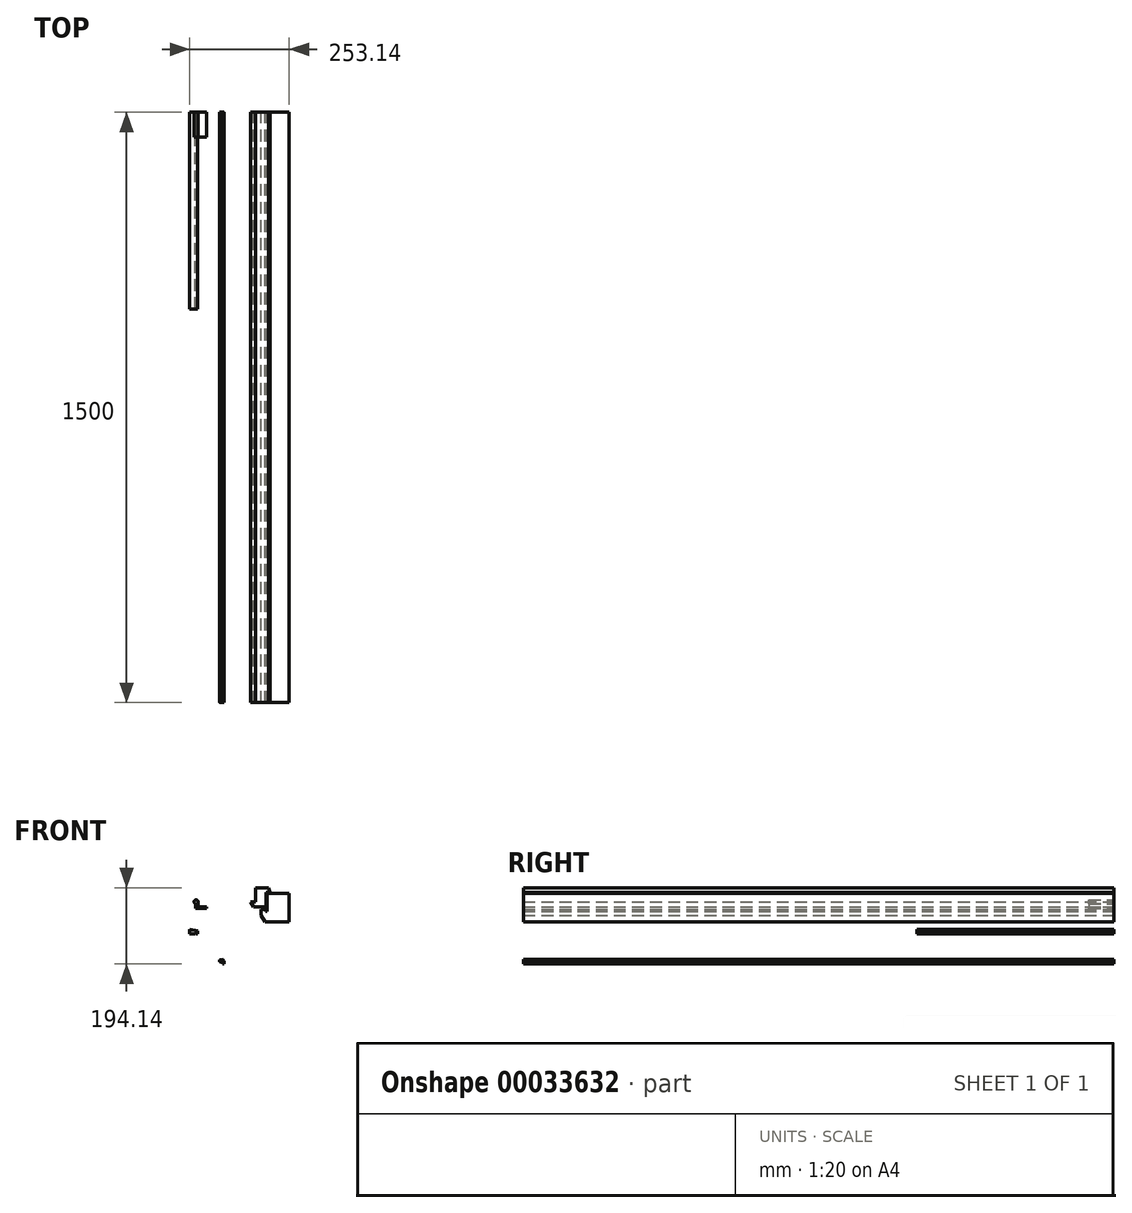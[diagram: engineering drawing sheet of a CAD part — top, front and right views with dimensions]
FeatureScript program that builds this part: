
annotation { "Feature Type Name" : "Feature", "Feature Type Description" : "" }
export const myFeature = defineFeature(function(context is Context, id is Id, definition is map)
    precondition{}
    {
        {
            var Q0;
            Q0=qCreatedBy(makeId("Front.planeOp"),FACE);
            var sketch = newSketch(context, id + "F0", { "sketchPlane" : qUnion([Q0])});
            skLineSegment(sketch, "E0.bottom", {"start": v(-57, 72) * mm, "end": v(0, 72) * mm});
            skLineSegment(sketch, "E0.top", {"start": v(-62, 0) * mm, "end": v(0, 0) * mm});
            skLineSegment(sketch, "E0.left", {"start": v(-72, 32) * mm, "end": v(-72, 17) * mm});
            skLineSegment(sketch, "E0.right", {"start": v(0, 72) * mm, "end": v(0, 0) * mm});
            skLineSegment(sketch, "E1.top", {"start": v(-72, 32) * mm, "end": v(-60, 32) * mm});
            skLineSegment(sketch, "E1.right", {"start": v(-57, 72) * mm, "end": v(-57, 32) * mm});
            skLineSegment(sketch, "E2", {"start": v(-72, 17) * mm, "end": v(-62, 0) * mm});
            skLineSegment(sketch, "E3", {"start": v(-57, 32) * mm, "end": v(-57, 26.5) * mm});
            skLineSegment(sketch, "E4", {"start": v(-57, 26.5) * mm, "end": v(-60, 26.5) * mm});
            skLineSegment(sketch, "E5", {"start": v(-60, 26.5) * mm, "end": v(-60, 32) * mm});
            skSolve(sketch);
        }
        {
            var Q0;
            Q0=qCreatedBy(makeId("Front.planeOp"),FACE);
            var sketch = newSketch(context, id + "F1", { "sketchPlane" : qUnion([Q0])});
            skLineSegment(sketch, "E6", {"start": v(-49, 75) * mm, "end": v(-59, 75) * mm});
            skLineSegment(sketch, "E7", {"start": v(-59, 75) * mm, "end": v(-59, 38) * mm});
            skLineSegment(sketch, "E8", {"start": v(-59, 38) * mm, "end": v(-91, 38) * mm});
            skLineSegment(sketch, "E9", {"start": v(-91, 38) * mm, "end": v(-98, 51) * mm});
            skLineSegment(sketch, "E10", {"start": v(-98, 51) * mm, "end": v(-86, 51) * mm});
            skLineSegment(sketch, "E11", {"start": v(-86, 51) * mm, "end": v(-86, 87) * mm});
            skLineSegment(sketch, "E12", {"start": v(-86, 87) * mm, "end": v(-53, 87) * mm});
            skLineSegment(sketch, "E13.0", {"start": v(-72, 38) * mm, "end": v(-57, 38) * mm, "construction": true});
            skLineSegment(sketch, "E14.0", {"start": v(-59, 72) * mm, "end": v(-59, 27) * mm, "construction": true});
            skLineSegment(sketch, "E15", {"start": v(-49, 75) * mm, "end": v(-53, 87) * mm});
            skSolve(sketch);
        }
        {
            var Q0;
            Q0=qCreatedBy(makeId("Front.planeOp"),FACE);
            var sketch = newSketch(context, id + "F2", { "sketchPlane" : qUnion([Q0])});
            skArc(sketch, "E16", {"start": v(-235.9, 46.13) * mm, "mid": v(-234.42, 46.6) * mm, "end": v(-233.15, 47.5) * mm});
            skLineSegment(sketch, "E17.0", {"start": v(-235.9, 46.13) * mm, "end": v(-235.9, 36.02) * mm});
            skLineSegment(sketch, "E18.0", {"start": v(-237.4, 46.13) * mm, "end": v(-237.4, 34.08) * mm});
            skLineSegment(sketch, "E19.0", {"start": v(-237.4, 34.08) * mm, "end": v(-210.4, 34.08) * mm});
            skLineSegment(sketch, "E20.0", {"start": v(-235.9, 36.02) * mm, "end": v(-210.4, 36.02) * mm});
            skLineSegment(sketch, "E21", {"start": v(-231.65, 51.08) * mm, "end": v(-231.65, 38.08) * mm});
            skLineSegment(sketch, "E22.trimOffspring", {"start": v(-231.65, 38.08) * mm, "end": v(-210.4, 38.08) * mm});
            skLineSegment(sketch, "E23", {"start": v(-210.4, 34.08) * mm, "end": v(-210.4, 36.02) * mm});
            skLineSegment(sketch, "E24.0", {"start": v(-233.15, 47.5) * mm, "end": v(-233.15, 36.58) * mm});
            skLineSegment(sketch, "E25.0", {"start": v(-233.15, 36.58) * mm, "end": v(-210.4, 36.58) * mm});
            skLineSegment(sketch, "E26", {"start": v(-210.4, 38.08) * mm, "end": v(-210.4, 36.58) * mm});
            skArc(sketch, "E27.trimOffspring", {"start": v(-231.65, 51.08) * mm, "mid": v(-239.9, 54.87) * mm, "end": v(-237.4, 46.13) * mm});
            skSolve(sketch);
        }
        {
            var Q0;
            Q0=makeQuery(id+"F0.imprint","IMPRINT",FACE,{"disambiguationData":[TD([[makeQuery(id+"F0.imprint","IMPRINT",EDGE,{"derivedFrom":sQuery(id+"F0.wireOp",EDGE,"E0.bottom")}),-1.0]])]});
            var Q1;
            Q1=makeQuery(id+"F1.imprint","IMPRINT",FACE,{"disambiguationData":[TD([[makeQuery(id+"F1.imprint","IMPRINT",EDGE,{"derivedFrom":sQuery(id+"F1.wireOp",EDGE,"E6")}),-1.0]])]});
            extrude(context, id + "F3", {"entities" : qUnion([Q0, Q1]), "depth" : 1500 * mm});
        }
        {
            var Q0;
            Q0=makeQuery(id+"F2.imprint","IMPRINT",FACE,{"disambiguationData":[TD([[makeQuery(id+"F2.imprint","IMPRINT",EDGE,{"derivedFrom":sQuery(id+"F2.wireOp",EDGE,"E16")}),1.0]])]});
            extrude(context, id + "F4", {"entities" : qUnion([Q0]), "depth" : 63 * mm});
        }
        {
            var Q0;
            Q0=qCreatedBy(makeId("Front.planeOp"),FACE);
            var sketch = newSketch(context, id + "F5", { "sketchPlane" : qUnion([Q0])});
            skLineSegment(sketch, "E28", {"start": v(-169.24, -107.14) * mm, "end": v(-166.24, -107.14) * mm});
            skLineSegment(sketch, "E29", {"start": v(-166.24, -107.14) * mm, "end": v(-166.24, -99.64) * mm});
            skLineSegment(sketch, "E30", {"start": v(-166.74, -99.14) * mm, "end": v(-173.95, -99.14) * mm});
            skLineSegment(sketch, "E31", {"start": v(-173.95, -99.14) * mm, "end": v(-168.15, -98.2) * mm});
            skLineSegment(sketch, "E32", {"start": v(-167.73, -97.62) * mm, "end": v(-167.98, -96.14) * mm});
            skLineSegment(sketch, "E33", {"start": v(-168.55, -95.72) * mm, "end": v(-176.52, -97.03) * mm});
            skLineSegment(sketch, "E34", {"start": v(-176.94, -97.52) * mm, "end": v(-176.94, -101.14) * mm});
            skLineSegment(sketch, "E35", {"start": v(-176.44, -101.64) * mm, "end": v(-169.24, -101.64) * mm});
            skLineSegment(sketch, "E36", {"start": v(-169.24, -101.64) * mm, "end": v(-169.24, -107.14) * mm});
            skPoint(sketch, "E37.visualSharp", {"position": v(-166.24, -99.14) * mm});
            skArc(sketch, "E37.filletArc", {"start": v(-166.24, -99.64) * mm, "mid": v(-166.39, -99.29) * mm, "end": v(-166.74, -99.14) * mm});
            skPoint(sketch, "E38.visualSharp", {"position": v(-167.65, -98.1) * mm});
            skArc(sketch, "E38.filletArc", {"start": v(-168.15, -98.2) * mm, "mid": v(-167.82, -97.99) * mm, "end": v(-167.73, -97.62) * mm});
            skPoint(sketch, "E39.visualSharp", {"position": v(-168.06, -95.64) * mm});
            skArc(sketch, "E39.filletArc", {"start": v(-167.98, -96.14) * mm, "mid": v(-168.18, -95.81) * mm, "end": v(-168.55, -95.72) * mm});
            skPoint(sketch, "E40.visualSharp", {"position": v(-176.94, -97.1) * mm});
            skArc(sketch, "E40.filletArc", {"start": v(-176.52, -97.03) * mm, "mid": v(-176.82, -97.2) * mm, "end": v(-176.94, -97.52) * mm});
            skPoint(sketch, "E41.visualSharp", {"position": v(-176.94, -101.64) * mm});
            skArc(sketch, "E41.filletArc", {"start": v(-176.94, -101.14) * mm, "mid": v(-176.8, -101.5) * mm, "end": v(-176.44, -101.64) * mm});
            skSolve(sketch);
        }
        {
            var Q0;
            Q0 = qSketchRegion(id + "F5", true);
            extrude(context, id + "F6", {"entities" : qUnion([Q0]), "depth" : 1500 * mm});
        }
        {
            var Q0;
            Q0=qCreatedBy(makeId("Front.planeOp"),FACE);
            var sketch = newSketch(context, id + "F7", { "sketchPlane" : qUnion([Q0])});
            skLineSegment(sketch, "E42", {"start": v(-253.14, -18.72) * mm, "end": v(-253.14, -30.72) * mm});
            skLineSegment(sketch, "E43", {"start": v(-253.14, -30.72) * mm, "end": v(-239.14, -30.72) * mm});
            skLineSegment(sketch, "E44", {"start": v(-233.14, -30.72) * mm, "end": v(-233.14, -22.82) * mm});
            skLineSegment(sketch, "E45", {"start": v(-233.14, -22.82) * mm, "end": v(-253.14, -18.72) * mm});
            skLineSegment(sketch, "E46", {"start": v(-236.14, -30.72) * mm, "end": v(-236.14, -27.72) * mm});
            skLineSegment(sketch, "E47", {"start": v(-236.14, -27.72) * mm, "end": v(-239.14, -27.72) * mm});
            skLineSegment(sketch, "E48", {"start": v(-239.14, -27.72) * mm, "end": v(-239.14, -30.72) * mm});
            skLineSegment(sketch, "E49.trimOffspring", {"start": v(-236.14, -30.72) * mm, "end": v(-233.14, -30.72) * mm});
            skSolve(sketch);
        }
        {
            var Q0;
            Q0 = qSketchRegion(id + "F7", true);
            extrude(context, id + "F8", {"entities" : qUnion([Q0]), "depth" : 500 * mm});
        }
    });
